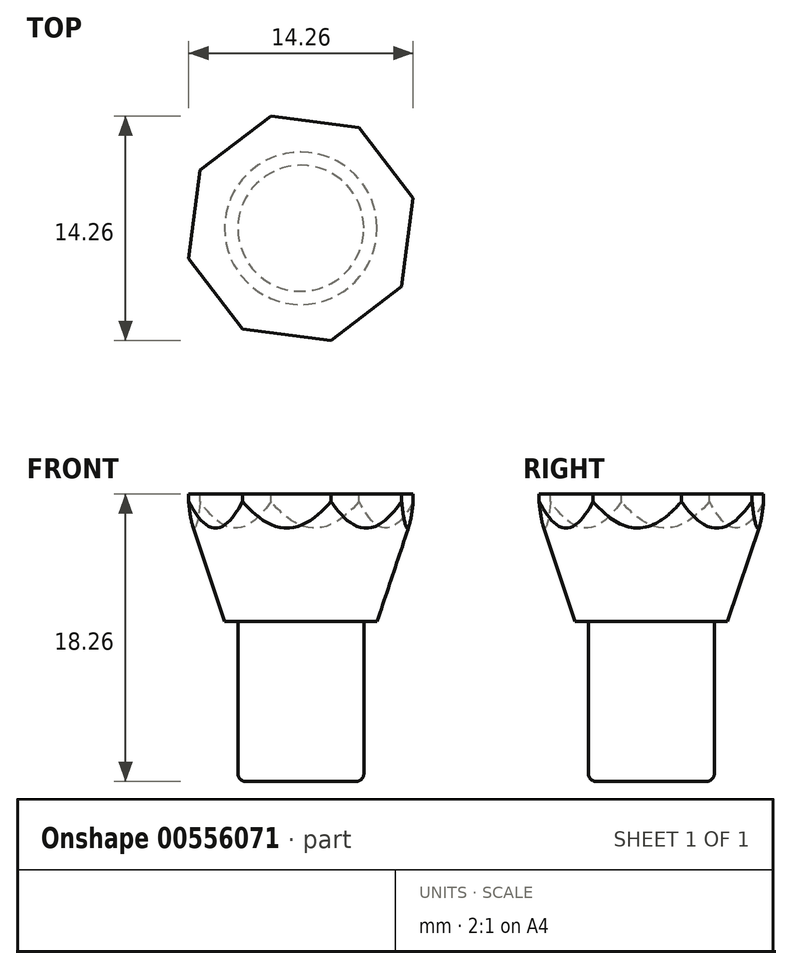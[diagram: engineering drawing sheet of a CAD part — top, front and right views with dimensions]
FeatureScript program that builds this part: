
annotation { "Feature Type Name" : "Feature", "Feature Type Description" : "" }
export const myFeature = defineFeature(function(context is Context, id is Id, definition is map)
    precondition{}
    {
        {
            var Q0;
            Q0=qCreatedBy(makeId("Top.planeOp"),FACE);
            var sketch = newSketch(context, id + "F0", { "sketchPlane" : qUnion([Q0])});
            skCircle(sketch, "E0", {"center": v(0, 0) * mm, "radius": 4 * mm});
            skCircle(sketch, "E1", {"center": v(0, 0) * mm, "radius": 7.38 * mm});
            skSolve(sketch);
        }
        {
            var Q0;
            Q0=makeQuery(id+"F0.imprint","IMPRINT",FACE,{"disambiguationData":[TD([[makeQuery(id+"F0.imprint","IMPRINT",EDGE,{"derivedFrom":sQuery(id+"F0.wireOp",EDGE,"E0")}),1.0]])]});
            extrude(context, id + "F1", {"entities" : qUnion([Q0]), "oppositeDirection" : true, "depth" : 10.16 * mm, "offsetDistance" : 25.4 * mm});
        }
        {
            var Q0;
            Q0=makeQuery(id+"F0.imprint","IMPRINT",FACE,{"disambiguationData":[TD([[makeQuery(id+"F0.imprint","IMPRINT",EDGE,{"derivedFrom":sQuery(id+"F0.wireOp",EDGE,"E0")}),-1.0]])]});
            var Q1;
            Q1=makeQuery(id+"F0.imprint","IMPRINT",FACE,{"disambiguationData":[TD([[makeQuery(id+"F0.imprint","IMPRINT",EDGE,{"derivedFrom":sQuery(id+"F0.wireOp",EDGE,"E0")}),1.0]])]});
            extrude(context, id + "F2", {"entities" : qUnion([Q0, Q1]), "operationType" : NewBodyOperationType.ADD, "depth" : 8.1 * mm, "offsetDistance" : 25.4 * mm});
        }
        {
            var Q0;
            Q0=makeQuery(id+"F2.opExtrude","CAP_EDGE",EDGE,{"disambiguationData":[OSD([sQuery(id+"F0.wireOp",EDGE,"E1")])],"isStart":true});
            chamfer(context, id + "F3", {"entities" : qUnion([Q0]), "chamferType" : ChamferType.TWO_OFFSETS, "width1" : 7.62 * mm, "oppositeDirection" : false, "width2" : 2.54 * mm, "tangentPropagation" : true});
        }
        {
            var Q0;
            Q0=makeQuery(id+"F2.opExtrude","CAP_FACE",FACE,{"disambiguationData":[OSD([sQuery(id+"F0.wireOp",EDGE,"E1")])],"isStart":false});
            var sketch = newSketch(context, id + "F4", { "sketchPlane" : qUnion([Q0])});
            skCircle(sketch, "E2.cCircle", {"center": v(0, 0) * mm, "radius": 7.38 * mm, "construction": true});
            skLineSegment(sketch, "E2.0", {"start": v(6.4, -3.7) * mm, "end": v(1.9, -7.13) * mm});
            skLineSegment(sketch, "E2.1", {"start": v(1.9, -7.13) * mm, "end": v(-3.7, -6.4) * mm});
            skLineSegment(sketch, "E2.2", {"start": v(-3.7, -6.4) * mm, "end": v(-7.13, -1.9) * mm});
            skLineSegment(sketch, "E2.3", {"start": v(-7.13, -1.9) * mm, "end": v(-6.4, 3.7) * mm});
            skLineSegment(sketch, "E2.4", {"start": v(-6.4, 3.7) * mm, "end": v(-1.9, 7.13) * mm});
            skLineSegment(sketch, "E2.5", {"start": v(-1.9, 7.13) * mm, "end": v(3.7, 6.4) * mm});
            skLineSegment(sketch, "E2.6", {"start": v(3.7, 6.4) * mm, "end": v(7.13, 1.9) * mm});
            skLineSegment(sketch, "E2.7", {"start": v(7.13, 1.9) * mm, "end": v(6.4, -3.7) * mm});
            skSolve(sketch);
        }
        {
            var Q0;
            {var subQ0=sQuery(id+"F4.wireOp",EDGE,"E2.4");Q0=makeQuery(id+"F4.imprint","IMPRINT",FACE,{"disambiguationData":[TD([[makeQuery(id+"F4.imprint","IMPRINT",EDGE,{"derivedFrom":subQ0}),1.0]])]});}
            var Q1;
            {var subQ0=sQuery(id+"F4.wireOp",EDGE,"E2.5");Q1=makeQuery(id+"F4.imprint","IMPRINT",FACE,{"disambiguationData":[TD([[makeQuery(id+"F4.imprint","IMPRINT",EDGE,{"derivedFrom":subQ0}),1.0]])]});}
            var Q2;
            {var subQ0=sQuery(id+"F4.wireOp",EDGE,"E2.6");Q2=makeQuery(id+"F4.imprint","IMPRINT",FACE,{"disambiguationData":[TD([[makeQuery(id+"F4.imprint","IMPRINT",EDGE,{"derivedFrom":subQ0}),1.0]])]});}
            var Q3;
            {var subQ0=sQuery(id+"F4.wireOp",EDGE,"E2.7");Q3=makeQuery(id+"F4.imprint","IMPRINT",FACE,{"disambiguationData":[TD([[makeQuery(id+"F4.imprint","IMPRINT",EDGE,{"derivedFrom":subQ0}),1.0]])]});}
            var Q4;
            {var subQ0=sQuery(id+"F4.wireOp",EDGE,"E2.0");Q4=makeQuery(id+"F4.imprint","IMPRINT",FACE,{"disambiguationData":[TD([[makeQuery(id+"F4.imprint","IMPRINT",EDGE,{"derivedFrom":subQ0}),1.0]])]});}
            var Q5;
            {var subQ0=sQuery(id+"F4.wireOp",EDGE,"E2.1");Q5=makeQuery(id+"F4.imprint","IMPRINT",FACE,{"disambiguationData":[TD([[makeQuery(id+"F4.imprint","IMPRINT",EDGE,{"derivedFrom":subQ0}),1.0]])]});}
            var Q6;
            {var subQ0=sQuery(id+"F4.wireOp",EDGE,"E2.2");Q6=makeQuery(id+"F4.imprint","IMPRINT",FACE,{"disambiguationData":[TD([[makeQuery(id+"F4.imprint","IMPRINT",EDGE,{"derivedFrom":subQ0}),1.0]])]});}
            var Q7;
            {var subQ0=sQuery(id+"F4.wireOp",EDGE,"E2.3");Q7=makeQuery(id+"F4.imprint","IMPRINT",FACE,{"disambiguationData":[TD([[makeQuery(id+"F4.imprint","IMPRINT",EDGE,{"derivedFrom":subQ0}),1.0]])]});}
            extrude(context, id + "F5", {"entities" : qUnion([Q0, Q1, Q2, Q3, Q4, Q5, Q6, Q7]), "operationType" : NewBodyOperationType.REMOVE, "oppositeDirection" : true, "depth" : 25.4 * mm, "offsetDistance" : 25.4 * mm});
        }
        {
            var Q0;
            Q0=makeQuery(id+"F1.opExtrude","CAP_EDGE",EDGE,{"disambiguationData":[OSD([sQuery(id+"F0.wireOp",EDGE,"E0")])],"isStart":false});
            fillet(context, id + "F6", {"entities" : qUnion([Q0]), "radius" : 0.5 * mm, "tangentPropagation" : true, "allowEdgeOverflow" : false});
        }
    });
